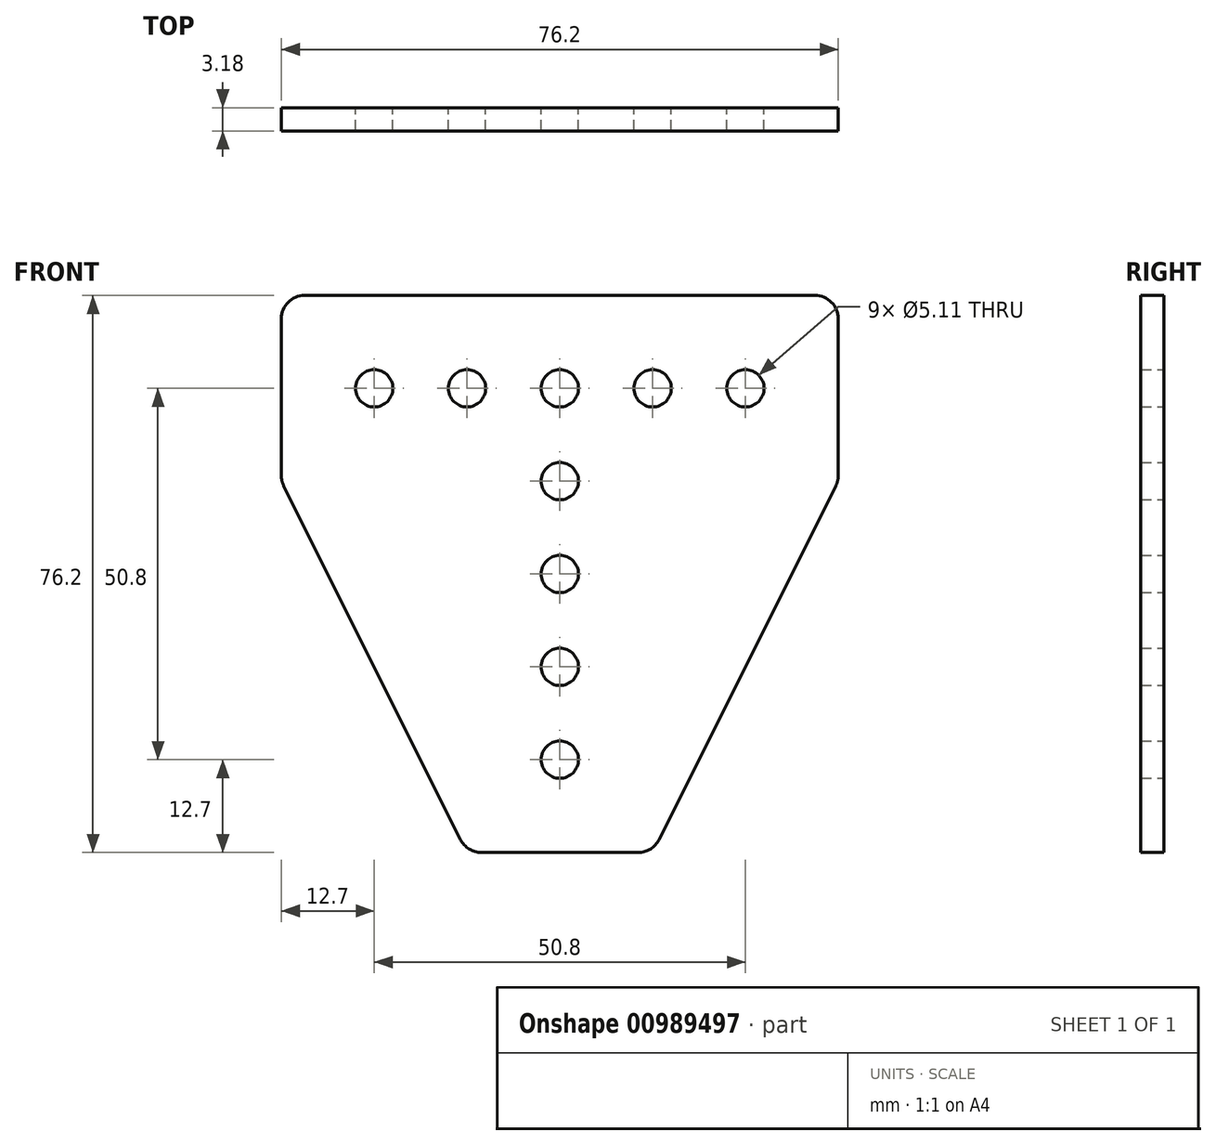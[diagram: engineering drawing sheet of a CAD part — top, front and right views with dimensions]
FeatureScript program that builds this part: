
annotation { "Feature Type Name" : "Feature", "Feature Type Description" : "" }
export const myFeature = defineFeature(function(context is Context, id is Id, definition is map)
    precondition{}
    {
        {
            var Q0;
            Q0=qCreatedBy(makeId("Front.planeOp"),FACE);
            var sketch = newSketch(context, id + "F0", { "sketchPlane" : qUnion([Q0])});
            skCircle(sketch, "E0", {"center": v(0, 0) * mm, "radius": 2.55 * mm});
            skCircle(sketch, "E1", {"center": v(-25.4, 0) * mm, "radius": 2.55 * mm});
            skCircle(sketch, "E2", {"center": v(-12.7, 0) * mm, "radius": 2.55 * mm});
            skCircle(sketch, "E3", {"center": v(12.7, 0) * mm, "radius": 2.55 * mm});
            skCircle(sketch, "E4", {"center": v(25.4, 0) * mm, "radius": 2.55 * mm});
            skCircle(sketch, "E5", {"center": v(0, -12.7) * mm, "radius": 2.55 * mm});
            skCircle(sketch, "E6", {"center": v(0, -25.4) * mm, "radius": 2.55 * mm});
            skLineSegment(sketch, "E7", {"start": v(-38.1, 12.7) * mm, "end": v(38.1, 12.7) * mm});
            skLineSegment(sketch, "E8", {"start": v(38.1, 12.7) * mm, "end": v(38.1, -12.7) * mm});
            skLineSegment(sketch, "E9", {"start": v(38.1, -12.7) * mm, "end": v(12.7, -63.5) * mm});
            skLineSegment(sketch, "E10", {"start": v(12.7, -63.5) * mm, "end": v(-12.7, -63.5) * mm});
            skLineSegment(sketch, "E11", {"start": v(-12.7, -63.5) * mm, "end": v(-38.1, -12.7) * mm});
            skLineSegment(sketch, "E12", {"start": v(-38.1, -12.7) * mm, "end": v(-38.1, 12.7) * mm});
            skPoint(sketch, "E13", {"position": v(0, -63.5) * mm});
            skCircle(sketch, "E14", {"center": v(0, -38.1) * mm, "radius": 2.55 * mm});
            skCircle(sketch, "E15", {"center": v(0, -50.8) * mm, "radius": 2.55 * mm});
            skSolve(sketch);
        }
        {
            var Q0;
            Q0 = qSketchRegion(id + "F0", true);
            extrude(context, id + "F1", {"entities" : qUnion([Q0]), "depth" : 3.17 * mm, "offsetDistance" : 25.4 * mm});
        }
        {
            var Q0;
            Q0=makeQuery(id+"F1.opExtrude","SWEPT_EDGE",EDGE,{"disambiguationData":[OSD([sQuery(id+"F0.wireOp",EDGE,"E7"),sQuery(id+"F0.wireOp",EDGE,"E8")])]});
            var Q1;
            Q1=makeQuery(id+"F1.opExtrude","SWEPT_EDGE",EDGE,{"disambiguationData":[OSD([sQuery(id+"F0.wireOp",EDGE,"E8"),sQuery(id+"F0.wireOp",EDGE,"E9")])]});
            var Q2;
            Q2=makeQuery(id+"F1.opExtrude","SWEPT_EDGE",EDGE,{"disambiguationData":[OSD([sQuery(id+"F0.wireOp",EDGE,"E9"),sQuery(id+"F0.wireOp",EDGE,"E10")])]});
            var Q3;
            Q3=makeQuery(id+"F1.opExtrude","SWEPT_EDGE",EDGE,{"disambiguationData":[OSD([sQuery(id+"F0.wireOp",EDGE,"E10"),sQuery(id+"F0.wireOp",EDGE,"E11")])]});
            var Q4;
            Q4=makeQuery(id+"F1.opExtrude","SWEPT_EDGE",EDGE,{"disambiguationData":[OSD([sQuery(id+"F0.wireOp",EDGE,"E11"),sQuery(id+"F0.wireOp",EDGE,"E12")])]});
            var Q5;
            Q5=makeQuery(id+"F1.opExtrude","SWEPT_EDGE",EDGE,{"disambiguationData":[OSD([sQuery(id+"F0.wireOp",EDGE,"E7"),sQuery(id+"F0.wireOp",EDGE,"E12")])]});
            fillet(context, id + "F2", {"entities" : qUnion([Q0, Q1, Q2, Q3, Q4, Q5]), "radius" : 3.17 * mm, "tangentPropagation" : true, "allowEdgeOverflow" : false});
        }
    });
